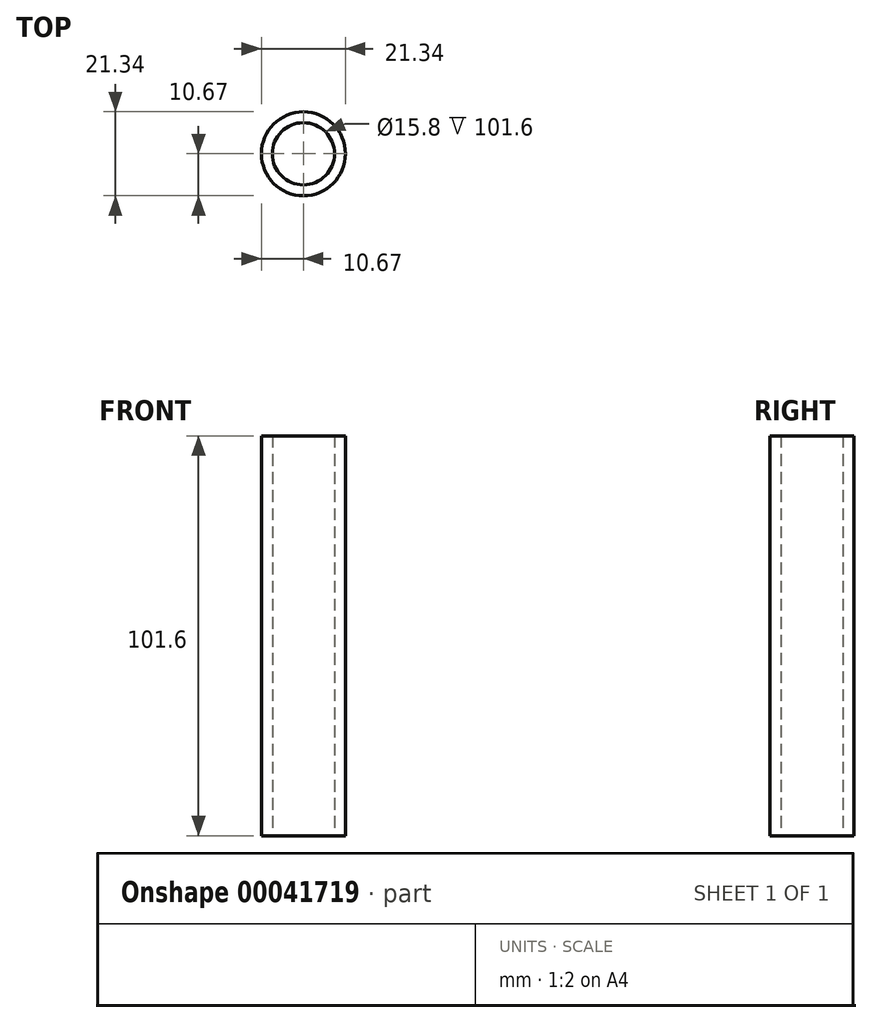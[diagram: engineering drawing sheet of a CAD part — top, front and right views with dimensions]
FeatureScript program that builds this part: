
annotation { "Feature Type Name" : "Feature", "Feature Type Description" : "" }
export const myFeature = defineFeature(function(context is Context, id is Id, definition is map)
    precondition{}
    {
        {
            var Q0;
            Q0=qCreatedBy(makeId("Top.planeOp"),FACE);
            var sketch = newSketch(context, id + "F0", { "sketchPlane" : qUnion([Q0])});
            skCircle(sketch, "E0", {"center": v(0, 0) * mm, "radius": 10.67 * mm});
            skSolve(sketch);
        }
        {
            var Q0;
            Q0=qSketchRegion(id+"F0",true);
            extrude(context, id + "F1", {"entities" : qUnion([Q0]), "depth" : 101.6 * mm});
        }
        {
            var Q0;
            Q0=qCreatedBy(makeId("Top.planeOp"),FACE);
            var sketch = newSketch(context, id + "F2", { "sketchPlane" : qUnion([Q0])});
            skCircle(sketch, "E1", {"center": v(0, 0) * mm, "radius": 7.9 * mm});
            skSolve(sketch);
        }
        {
            var Q0;
            Q0=qSketchRegion(id+"F2",true);
            extrude(context, id + "F3", {"entities" : qUnion([Q0]), "operationType" : NewBodyOperationType.REMOVE, "endBound" : BoundingType.THROUGH_ALL, "depth" : 304.8 * mm});
        }
    });
